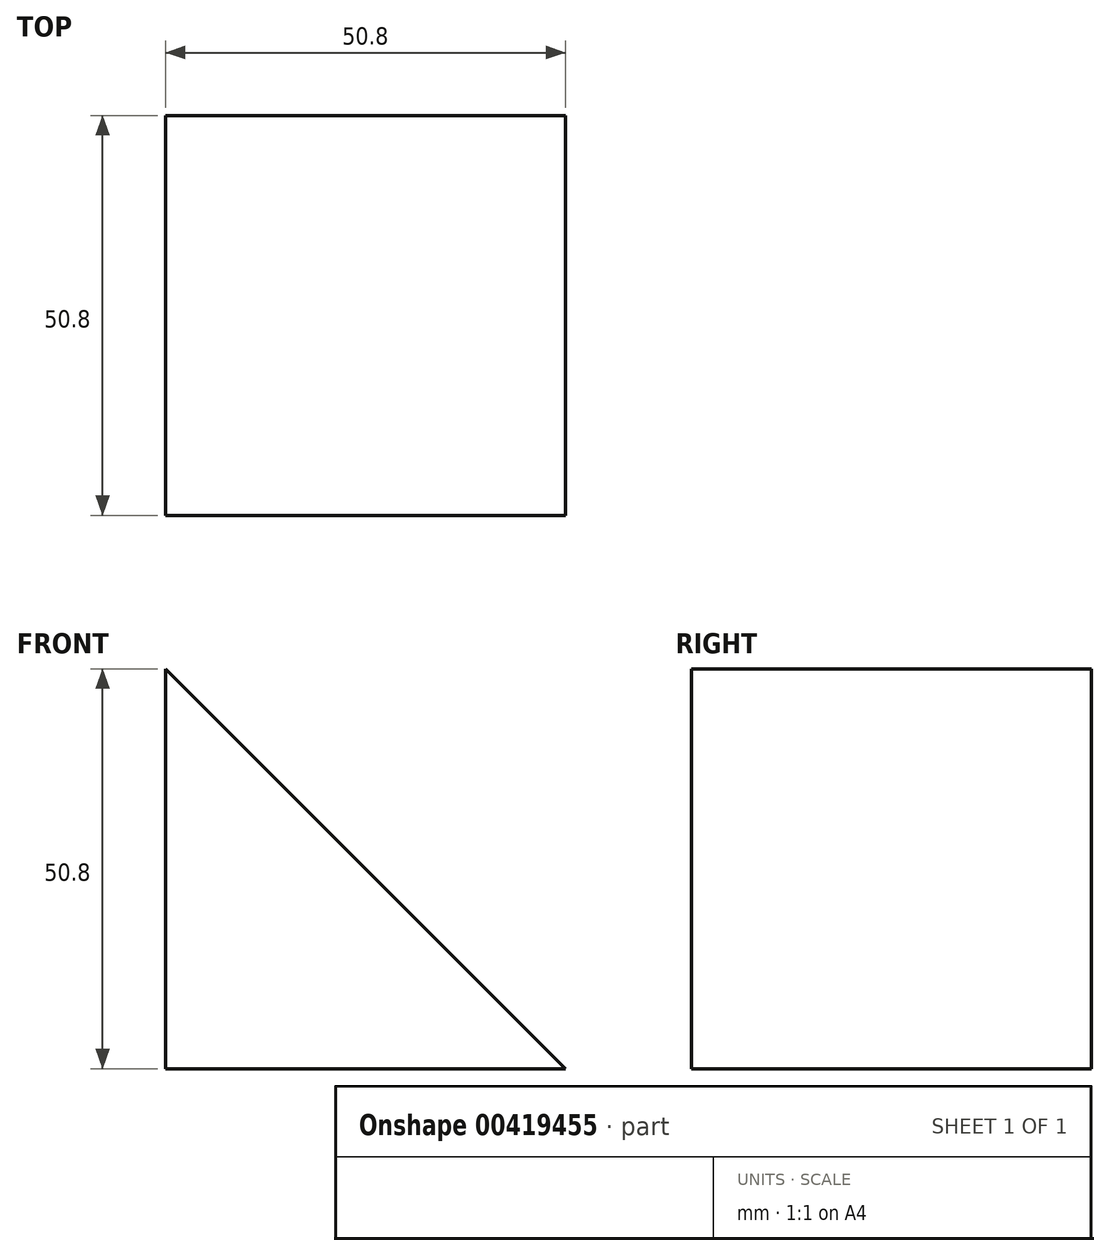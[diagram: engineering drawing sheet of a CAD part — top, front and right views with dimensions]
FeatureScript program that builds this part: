
annotation { "Feature Type Name" : "Feature", "Feature Type Description" : "" }
export const myFeature = defineFeature(function(context is Context, id is Id, definition is map)
    precondition{}
    {
        {
            var Q0;
            Q0=qCreatedBy(makeId("Front.planeOp"),FACE);
            var sketch = newSketch(context, id + "F0", { "sketchPlane" : qUnion([Q0])});
            skLineSegment(sketch, "E0", {"start": v(-41.39, 12.07) * mm, "end": v(-41.39, -38.73) * mm});
            skLineSegment(sketch, "E1", {"start": v(-41.39, -38.73) * mm, "end": v(9.41, -38.73) * mm});
            skLineSegment(sketch, "E2", {"start": v(9.41, -38.73) * mm, "end": v(-41.39, 12.07) * mm});
            skSolve(sketch);
        }
        {
            var Q0;
            Q0 = qSketchRegion(id + "F0", true);
            extrude(context, id + "F1", {"entities" : qUnion([Q0]), "depth" : 50.8 * mm});
        }
    });
